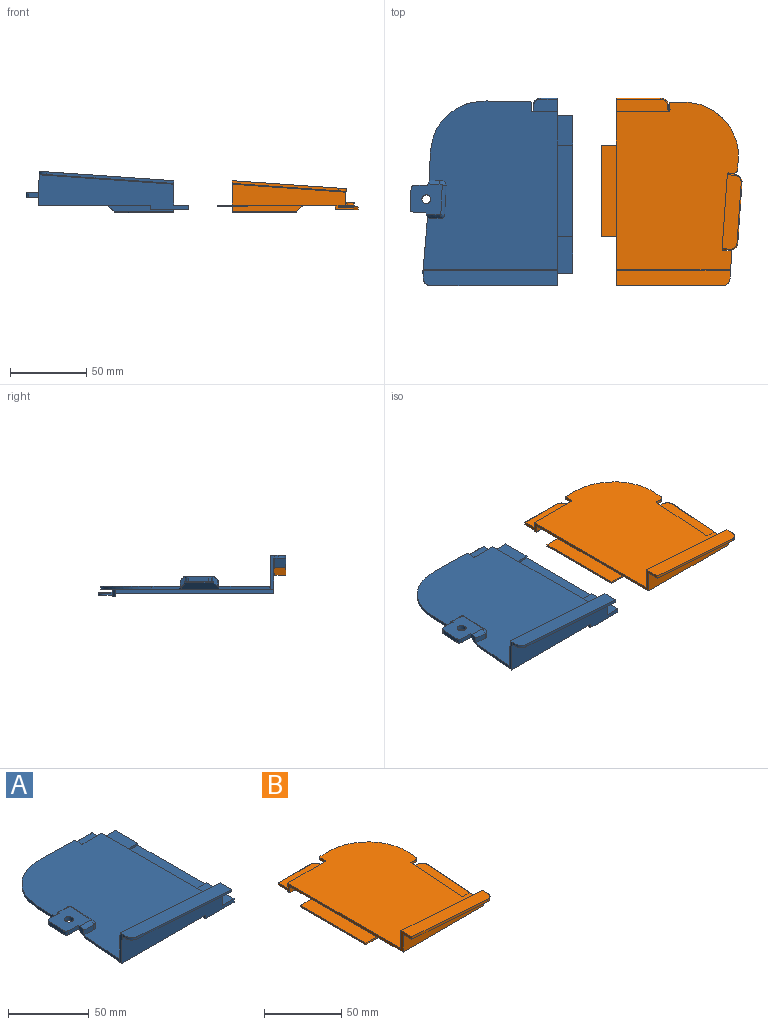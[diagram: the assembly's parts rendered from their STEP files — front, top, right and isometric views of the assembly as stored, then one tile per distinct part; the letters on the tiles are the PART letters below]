
ASSEMBLY  parts=2 mates=2
PART A: 73 faces, bbox 107.6x124.2x28 mm
  f0: plane 113.14x88.67mm, normal (0,0,-1), area 7242.1mm2, adj f1,f2,f4,f6,f8,f10,f20,f28
  f1: cylinder r=0.5mm len=28.53mm, axis (1,0,0), area 22.2mm2, adj f0,f9,f57,f63
  f2: plane 122.91x21.01mm, normal (1,0,0), area 259.8mm2, adj f0,f3,f5,f7,f8,f9,f10,f11
  f3: cylinder r=0.5mm len=88.44mm, axis (1,0,0), area 69.4mm2, adj f2,f4,f6,f7,f19,f28
  f4: cylinder r=0.5mm len=2.09mm, axis (0,0,-1), area 1.1mm2, adj f0,f3,f6,f28
  f5: plane 60x9.9mm, normal (0,0,-1), area 594mm2, adj f2,f67,f68,f69
  f6: plane 22.19x2.98mm, normal (-1,0.09,0.03), area 45.4mm2, adj f0,f3,f4,f19,f20,f21,f22,f24
  f7: plane 110.64x88.15mm, normal (0,0,1), area 8709mm2, adj f2,f3,f8,f28,f29,f30,f31,f32
  f8: plane 16.47x1.8mm, normal (0,1,0), area 29.6mm2, adj f0,f2,f7,f29
  f9: plane 43.03x4mm, normal (0,-1,0), area 131.1mm2, adj f1,f2,f16,f57,f63,f72
  f10: plane 43.53x4.5mm, normal (0,1,0), area 148.7mm2, adj f0,f2,f12,f18,f33,f57,f59
  f11: plane 38.53x1mm, normal (0,0,-1), area 38.5mm2, adj f2,f16,f18,f57
  f12: plane 15.61x8.5mm, normal (0,0,1), area 128.3mm2, adj f2,f10,f15,f59,f60
  f13: plane 16.11x8.5mm, normal (0,0,-1), area 131.6mm2, adj f2,f14,f17,f33,f58
  f14: plane 11.11x1.3mm, normal (0,1,0), area 14.4mm2, adj f2,f13,f15,f58
  f15: cylinder r=0.5mm len=11.11mm, axis (-1,0,0), area 8.7mm2, adj f2,f12,f14,f60
  f16: cylinder r=0.5mm len=39.03mm, axis (1,0,0), area 30.5mm2, adj f2,f9,f11,f57
  f17: cylinder r=0.5mm len=16.11mm, axis (1,0,0), area 12.7mm2, adj f2,f13,f18,f33
  f18: cylinder r=0.5mm len=39.03mm, axis (-1,0,0), area 30.5mm2, adj f2,f10,f11,f17,f57
  f19: plane 88.44x19.85mm, normal (0,1,0), area 1479.9mm2, adj f2,f3,f6,f21
  f20: plane 98.67x22.56mm, normal (0,-1,0), area 1551.6mm2, adj f0,f2,f6,f24,f63,f64,f66,f72
  f21: plane 88.1x10mm, normal (0.07,0,1), area 877.6mm2, adj f2,f6,f19,f23,f61,f62
  f22: plane 88.22x7.5mm, normal (-0.07,0,-1), area 657.9mm2, adj f2,f6,f23,f24,f61,f62
  f23: plane 83.23x7.62mm, normal (0,-1,0), area 150.1mm2, adj f2,f21,f22,f62
  f24: cylinder r=0.5mm len=88.26mm, axis (1,0,-0.07), area 69.4mm2, adj f2,f6,f20,f22
  f25: plane 8.75x3mm, normal (-0.05,-1,0), area 26.3mm2, adj f34,f36,f37,f48
  f26: plane 8.45x3mm, normal (0.05,1,0), area 25.4mm2, adj f34,f43,f44,f48
  f27: cylinder r=2.87mm len=5.74mm, axis (0,0,-1), area 54.1mm2, adj f34,f48
  f28: plane 34.08x2.83mm, normal (-1,0.08,0), area 60.4mm2, adj f0,f3,f4,f7,f37,f51
  f29: extruded ~6.63x1.92mm, area 14.4mm2, adj f0,f7,f8,f30
  f30: plane 28.52x1.8mm, normal (0.02,1,0), area 51.3mm2, adj f0,f7,f29,f31
  f31: extruded ~36.61x33.45mm, area 98.7mm2, adj f0,f7,f30,f32
  f32: plane 18.64x1.8mm, normal (-1,0.03,0), area 33mm2, adj f0,f7,f31,f43,f49
  f33: plane 4x1.8mm, normal (-1,0,0), area 5.3mm2, adj f10,f13,f17,f58,f59
  f34: plane 21.13x20.23mm, normal (0,0,1), area 350.6mm2, adj f25,f26,f27,f35,f36,f37,f43,f44
  f35: plane 13.13x3mm, normal (-1,0.05,0), area 39.5mm2, adj f34,f36,f44,f48
  f36: extruded ~3x2.08mm, area 8.9mm2, adj f25,f34,f35,f48
  f37: plane 7.37x4.38mm, normal (-0.96,-0.28,0), area 14.3mm2, adj f7,f25,f28,f34,f38,f47,f48,f51
  f38: plane 8.3x3.7mm, normal (-0.05,-1,0), area 30.7mm2, adj f7,f37,f39,f52
  f39: cylinder r=2.81mm len=3.7mm, axis (0,0,-1), area 16mm2, adj f7,f38,f40,f53
  f40: plane 18.83x3.7mm, normal (1,-0.05,0), area 69.8mm2, adj f7,f39,f41,f54
  f41: cylinder r=3.37mm len=4.34mm, axis (0,0,-1), area 23.8mm2, adj f7,f40,f42,f55
  f42: plane 6.44x3.7mm, normal (0.06,1,0), area 23.9mm2, adj f7,f41,f43,f56
  f43: plane 7.77x4.56mm, normal (-0.94,0.34,0), area 16.9mm2, adj f7,f26,f32,f34,f42,f45,f48,f49
  f44: extruded ~3x2.36mm, area 11mm2, adj f26,f34,f35,f48
  f45: plane 8.05x1mm, normal (-0.08,-1,0), area 8.1mm2, adj f43,f46,f48,f49
  f46: plane 18.67x1.08mm, normal (-1,0.06,0), area 18.7mm2, adj f45,f47,f48,f50
  f47: plane 7.99x1mm, normal (0.02,1,0), area 8mm2, adj f37,f46,f48,f51
  f48: plane 19.8x19.31mm, normal (0,0,-1), area 316.2mm2, adj f25,f26,f27,f35,f36,f37,f43,f44
  f49: plane 12.27x4.56mm, normal (-0.06,-0.7,-0.71), area 53.9mm2, adj f0,f32,f43,f45,f50
  f50: plane 26.42x5.3mm, normal (-0.71,0.04,-0.71), area 127.8mm2, adj f0,f46,f49,f51
  f51: plane 11.76x4.2mm, normal (0.01,0.71,-0.71), area 53.2mm2, adj f0,f28,f37,f47,f50
  f52: bspline ~9.26x2.93mm, area 31.2mm2, adj f34,f37,f38,f53
  f53: bspline ~2.95x2.84mm, area 9.1mm2, adj f34,f39,f52,f54
  f54: bspline ~19.89x3.44mm, area 67.2mm2, adj f34,f40,f53,f55
  f55: bspline ~5.51x3.57mm, area 16.3mm2, adj f34,f41,f54,f56
  f56: bspline ~8.7x2.98mm, area 25.5mm2, adj f34,f42,f43,f55
  f57: plane 5.21x5.21mm, normal (-0.71,0,-0.71), area 14.1mm2, adj f0,f1,f9,f10,f11,f16,f18
  f58: cylinder r=5mm len=5mm, axis (0,0,-1), area 10.2mm2, adj f13,f14,f33,f60
  f59: cylinder r=0.5mm len=4mm, axis (0,-1,0), area 3.1mm2, adj f10,f12,f33,f60
  f60: torus R=4.5mm, axis (0,0,1), area 5.9mm2, adj f12,f15,f58,f59
  f61: plane 3x1.8mm, normal (-1,0,0.07), area 4.6mm2, adj f6,f21,f22,f62
  f62: cylinder r=5mm len=5.11mm, axis (0.07,0,1), area 14.1mm2, adj f21,f22,f23,f61
  f63: plane 103.89x2.7mm, normal (-1,0,0), area 280.5mm2, adj f0,f1,f9,f20,f72
  f64: plane 24.25x10mm, normal (0,0,1), area 242.5mm2, adj f2,f20,f66,f69
  f65: plane 10x2.7mm, normal (0,1,0), area 27mm2, adj f2,f66,f70,f72
  f66: plane 103.89x2.7mm, normal (1,0,0), area 190.5mm2, adj f20,f64,f65,f67,f69,f70,f71,f72
  f67: plane 19.9x1.5mm, normal (0,-1,0), area 29.9mm2, adj f5,f66,f68,f70,f71
  f68: plane 60x1.5mm, normal (1,0,0), area 90mm2, adj f5,f67,f69,f71
  f69: plane 19.9x1.5mm, normal (0,1,0), area 29.9mm2, adj f5,f64,f66,f68,f71
  f70: plane 19.64x10mm, normal (0,0,1), area 196.4mm2, adj f2,f65,f66,f67
  f71: plane 60x19.9mm, normal (0,0,1), area 1194mm2, adj f66,f67,f68,f69
  f72: plane 103.89x25mm, normal (0,0,-1), area 2597.3mm2, adj f9,f20,f63,f65,f66
PART B: 59 faces, bbox 92.9x123.3x21 mm
  f0: plane 111.49x80.2mm, normal (0,0,1), area 7782.5mm2, adj f1,f2,f3,f4,f5,f6,f7,f8
  f1: plane 49.47x3.5mm, normal (1,-0.07,0), area 148.9mm2, adj f0,f4,f5,f18,f19,f22,f32,f36
  f2: plane 33.64x1.8mm, normal (0,1,0), area 60.6mm2, adj f0,f9,f10,f51
  f3: plane 13.45x1.8mm, normal (1,-0.07,0), area 24.1mm2, adj f0,f4,f10,f58
  f4: extruded ~6.49x1.8mm, area 12.2mm2, adj f0,f1,f3,f10
  f5: extruded ~6.71x2.54mm, area 14.7mm2, adj f0,f1,f6,f10
  f6: plane 7.62x1.8mm, normal (1,-0.07,0), area 13.8mm2, adj f0,f5,f7,f10
  f7: extruded ~36.96x35.12mm, area 102.2mm2, adj f0,f6,f8,f10
  f8: plane 8.98x1.8mm, normal (0,1,0), area 16.2mm2, adj f0,f7,f9,f10
  f9: extruded ~6.43x2.33mm, area 14.4mm2, adj f0,f2,f8,f10
  f10: plane 112.38x80.2mm, normal (0,0,-1), area 7127.3mm2, adj f2,f3,f4,f5,f6,f7,f8,f9
  f11: plane 45.97x4mm, normal (0,-1,0), area 175.9mm2, adj f25,f37,f41,f51
  f12: plane 46.47x4.5mm, normal (0,1,0), area 120.5mm2, adj f10,f14,f15,f25,f31,f39,f51
  f13: plane 41.47x1mm, normal (0,0,-1), area 41.5mm2, adj f25,f37,f39,f51
  f14: plane 33.68x8.5mm, normal (0,0,1), area 281.9mm2, adj f12,f29,f30,f31,f51
  f15: plane 4x1.8mm, normal (1,0,0), area 5.3mm2, adj f12,f16,f28,f31,f38
  f16: plane 34.18x8.5mm, normal (0,0,-1), area 285.1mm2, adj f15,f17,f28,f38,f51
  f17: plane 29.18x1.3mm, normal (0,1,0), area 37.9mm2, adj f16,f28,f29,f51
  f18: plane 7.48x3mm, normal (0.07,1,0), area 12.6mm2, adj f1,f10,f20,f21,f27,f32,f40
  f19: plane 3x2.49mm, normal (-0.07,-1,0), area 6.1mm2, adj f1,f10,f20,f21,f23,f40
  f20: plane 49.47x3.45mm, normal (-1,0.07,0), area 124mm2, adj f18,f19,f21,f40
  f21: plane 49.97x15.08mm, normal (0,0,-1), area 584.4mm2, adj f18,f19,f20,f23,f24,f26,f27
  f22: plane 48.83x12.55mm, normal (0,0,1), area 452.9mm2, adj f1,f32,f33,f34,f35,f36
  f23: plane 4.99x1.3mm, normal (-0.07,-1,0), area 6.5mm2, adj f19,f21,f26,f36
  f24: plane 39.5x2.75mm, normal (1,-0.07,0), area 51.5mm2, adj f21,f26,f27,f34
  f25: plane 5x5mm, normal (0.71,0,-0.71), area 14.1mm2, adj f10,f11,f12,f13,f37,f39,f41
  f26: cylinder r=5mm len=5.34mm, axis (0,0,1), area 10.2mm2, adj f21,f23,f24,f35
  f27: cylinder r=5mm len=5.34mm, axis (0,0,1), area 10.2mm2, adj f18,f21,f24,f33
  f28: cylinder r=5mm len=5mm, axis (0,0,1), area 10.2mm2, adj f15,f16,f17,f30
  f29: cylinder r=0.5mm len=29.18mm, axis (-1,0,0), area 22.9mm2, adj f14,f17,f30,f51
  f30: torus R=4.5mm, axis (0,0,1), area 5.9mm2, adj f14,f28,f29,f31
  f31: cylinder r=0.5mm len=4mm, axis (0,1,0), area 3.1mm2, adj f12,f14,f15,f30
  f32: cylinder r=0.5mm len=5.02mm, axis (-1,0.07,0), area 3.9mm2, adj f1,f18,f22,f33
  f33: torus R=4.5mm, axis (0,0,1), area 5.9mm2, adj f22,f27,f32,f34
  f34: cylinder r=0.5mm len=39.53mm, axis (0.07,1,0), area 31.1mm2, adj f22,f24,f33,f35
  f35: torus R=4.5mm, axis (0,0,1), area 5.9mm2, adj f22,f26,f34,f36
  f36: cylinder r=0.5mm len=5.02mm, axis (-1,0.07,0), area 3.9mm2, adj f1,f22,f23,f35
  f37: cylinder r=0.5mm len=41.97mm, axis (1,0,0), area 32.7mm2, adj f11,f13,f25,f51
  f38: cylinder r=0.5mm len=34.18mm, axis (1,0,0), area 26.8mm2, adj f15,f16,f39,f51
  f39: cylinder r=0.5mm len=41.97mm, axis (-1,0,0), area 32.7mm2, adj f12,f13,f25,f38,f51
  f40: cylinder r=0.5mm len=49.5mm, axis (-0.07,-1,0), area 38.9mm2, adj f10,f18,f19,f20
  f41: cylinder r=0.5mm len=46.47mm, axis (1,0,0), area 36.4mm2, adj f10,f11,f25,f51
  f42: plane 74.7x13.7mm, normal (0,1,0), area 825.8mm2, adj f44,f45,f50,f51
  f43: plane 74.54x13.69mm, normal (0,-1,0), area 824mm2, adj f10,f44,f49,f51
  f44: plane 10.79x5.51mm, normal (1,0,-0.07), area 25.1mm2, adj f0,f10,f42,f43,f45,f46,f48,f49
  f45: plane 74.7x10mm, normal (0.07,0,1), area 743.5mm2, adj f42,f44,f47,f48,f51
  f46: plane 74.58x7.5mm, normal (-0.07,0,-1), area 555.3mm2, adj f44,f47,f48,f49,f51
  f47: plane 69.72x6.67mm, normal (0,-1,0), area 125.7mm2, adj f45,f46,f48,f51
  f48: cylinder r=5mm len=5.11mm, axis (-0.07,0,-1), area 14.1mm2, adj f44,f45,f46,f47
  f49: cylinder r=0.5mm len=74.61mm, axis (1,0,-0.07), area 58.7mm2, adj f43,f44,f46,f51
  f50: cylinder r=0.5mm len=74.11mm, axis (1,0,0), area 58.2mm2, adj f0,f42,f44,f51
  f51: plane 122.91x21.01mm, normal (-1,0,0), area 259.9mm2, adj f0,f2,f10,f11,f12,f13,f14,f16
  f52: plane 60x10mm, normal (0,0,1), area 600mm2, adj f51,f53,f54,f55
  f53: plane 20x1.2mm, normal (0,-1,0), area 24mm2, adj f10,f52,f54,f56,f57
  f54: plane 60x1.2mm, normal (-1,0,0), area 72mm2, adj f52,f53,f55,f57
  f55: plane 20x1.2mm, normal (0,1,0), area 24mm2, adj f10,f52,f54,f56,f57
  f56: plane 60x1.2mm, normal (1,0,0), area 72mm2, adj f10,f53,f55,f57
  f57: plane 60x20mm, normal (0,0,-1), area 1200mm2, adj f53,f54,f55,f56
  f58: plane 1.8x0.97mm, normal (0.71,-0.71,-0.05), area 2.3mm2, adj f0,f3,f10,f44
PLACE A t=(8.12,-25.93,-9.56)mm
PLACE B t=(46.61,-25.93,-9.56)mm
MATE planar B.f42 <-> A.f19  axis (0,1,0) through (80.91,-78.18,-1.6)mm
MATE planar A.f7 <-> B.f0  axis (0,0,1) through (-32.6,-24.88,-7.76)mm
